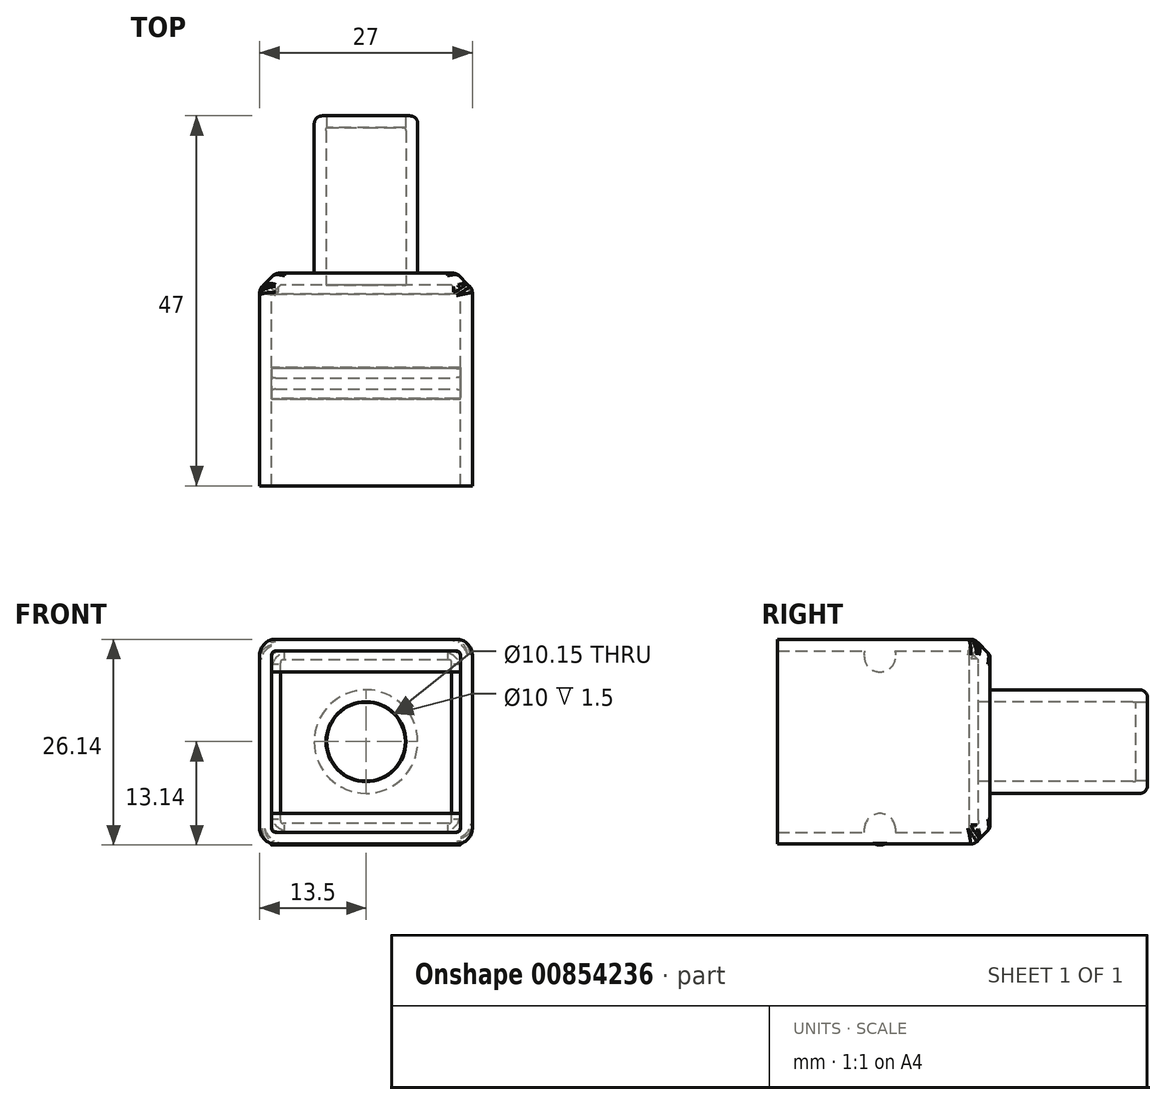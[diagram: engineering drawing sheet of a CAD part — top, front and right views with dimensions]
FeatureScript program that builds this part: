
annotation { "Feature Type Name" : "Feature", "Feature Type Description" : "" }
export const myFeature = defineFeature(function(context is Context, id is Id, definition is map)
    precondition{}
    {
        {
            var Q0;
            Q0=qCreatedBy(makeId("Front.planeOp"),FACE);
            var sketch = newSketch(context, id + "F0", { "sketchPlane" : qUnion([Q0])});
            skLineSegment(sketch, "E0.bottom", {"start": v(13.5, -13) * mm, "end": v(-13.5, -13) * mm});
            skLineSegment(sketch, "E0.top", {"start": v(13.5, 13) * mm, "end": v(-13.5, 13) * mm});
            skLineSegment(sketch, "E0.left", {"start": v(13.5, -13) * mm, "end": v(13.5, 13) * mm});
            skLineSegment(sketch, "E0.right", {"start": v(-13.5, -13) * mm, "end": v(-13.5, 13) * mm});
            skPoint(sketch, "E0.middle", {"position": v(0, 0) * mm});
            skSolve(sketch);
        }
        {
            var Q0;
            Q0=makeQuery(id+"F0.imprint","IMPRINT",FACE,{"disambiguationData":[TD([[makeQuery(id+"F0.imprint","IMPRINT",EDGE,{"derivedFrom":sQuery(id+"F0.wireOp",EDGE,"E0.bottom")}),-1.0]])]});
            extrude(context, id + "F1", {"entities" : qUnion([Q0]), "depth" : 27 * mm, "offsetDistance" : 25 * mm});
        }
        {
            var Q0;
            Q0=qCreatedBy(makeId("Front.planeOp"),FACE);
            var sketch = newSketch(context, id + "F2", { "sketchPlane" : qUnion([Q0])});
            skCircle(sketch, "E1", {"center": v(0, 0) * mm, "radius": 6.58 * mm});
            skSolve(sketch);
        }
        {
            var Q0;
            Q0=makeQuery(id+"F2.imprint","IMPRINT",FACE,{"disambiguationData":[TD([[makeQuery(id+"F2.imprint","IMPRINT",EDGE,{"derivedFrom":sQuery(id+"F2.wireOp",EDGE,"E1")}),1.0]])]});
            extrude(context, id + "F3", {"entities" : qUnion([Q0]), "operationType" : NewBodyOperationType.ADD, "oppositeDirection" : true, "depth" : 20 * mm, "offsetDistance" : 25 * mm});
        }
        {
            var Q0;
            Q0=makeQuery(id+"F3.opExtrude","CAP_EDGE",EDGE,{"disambiguationData":[OSD([sQuery(id+"F2.wireOp",EDGE,"E1")])],"isStart":false});
            fillet(context, id + "F4", {"entities" : qUnion([Q0]), "radius" : 1 * mm, "tangentPropagation" : true, "allowEdgeOverflow" : false});
        }
        {
            var Q0;
            Q0=makeQuery(id+"F1.opExtrude","CAP_EDGE",EDGE,{"disambiguationData":[OSD([sQuery(id+"F0.wireOp",EDGE,"E0.left")])],"isStart":true});
            var Q1;
            Q1=makeQuery(id+"F1.opExtrude","CAP_EDGE",EDGE,{"disambiguationData":[OSD([sQuery(id+"F0.wireOp",EDGE,"E0.bottom")])],"isStart":true});
            var Q2;
            Q2=makeQuery(id+"F1.opExtrude","CAP_EDGE",EDGE,{"disambiguationData":[OSD([sQuery(id+"F0.wireOp",EDGE,"E0.right")])],"isStart":true});
            var Q3;
            Q3=makeQuery(id+"F1.opExtrude","CAP_EDGE",EDGE,{"disambiguationData":[OSD([sQuery(id+"F0.wireOp",EDGE,"E0.top")])],"isStart":true});
            chamfer(context, id + "F5", {"entities" : qUnion([Q0, Q1, Q2, Q3]), "width" : 2 * mm, "tangentPropagation" : true});
        }
        {
            var Q0;
            {var subQ0=sQuery(id+"F0.wireOp",EDGE,"E0.right");Q0=makeQuery(id+"F5.opChamfer","BLEND_EDGE",EDGE,{"blendedFrom":[makeQuery(id+"F1.opExtrude","CAP_EDGE",EDGE,{"disambiguationData":[OSD([subQ0])],"isStart":true}),makeQuery(id+"F1.opExtrude","CAP_FACE",FACE,{"disambiguationData":[OSD([sQuery(id+"F0.wireOp",EDGE,"E0.bottom"),sQuery(id+"F0.wireOp",EDGE,"E0.top"),sQuery(id+"F0.wireOp",EDGE,"E0.left"),subQ0])],"isStart":true})],"blendedInto":[makeQuery(id+"F1.opExtrude","CAP_FACE",FACE,{"disambiguationData":[OSD([sQuery(id+"F0.wireOp",EDGE,"E0.bottom"),sQuery(id+"F0.wireOp",EDGE,"E0.top"),sQuery(id+"F0.wireOp",EDGE,"E0.left"),subQ0])],"isStart":true})]});}
            var Q1;
            {var subQ0=sQuery(id+"F0.wireOp",EDGE,"E0.bottom");Q1=makeQuery(id+"F5.opChamfer","BLEND_EDGE",EDGE,{"blendedFrom":[makeQuery(id+"F1.opExtrude","CAP_EDGE",EDGE,{"disambiguationData":[OSD([subQ0])],"isStart":true}),makeQuery(id+"F1.opExtrude","CAP_FACE",FACE,{"disambiguationData":[OSD([subQ0,sQuery(id+"F0.wireOp",EDGE,"E0.top"),sQuery(id+"F0.wireOp",EDGE,"E0.left"),sQuery(id+"F0.wireOp",EDGE,"E0.right")])],"isStart":true})],"blendedInto":[makeQuery(id+"F1.opExtrude","CAP_FACE",FACE,{"disambiguationData":[OSD([subQ0,sQuery(id+"F0.wireOp",EDGE,"E0.top"),sQuery(id+"F0.wireOp",EDGE,"E0.left"),sQuery(id+"F0.wireOp",EDGE,"E0.right")])],"isStart":true})]});}
            var Q2;
            {var subQ0=sQuery(id+"F0.wireOp",EDGE,"E0.left");Q2=makeQuery(id+"F5.opChamfer","BLEND_EDGE",EDGE,{"blendedFrom":[makeQuery(id+"F1.opExtrude","CAP_EDGE",EDGE,{"disambiguationData":[OSD([subQ0])],"isStart":true}),makeQuery(id+"F1.opExtrude","CAP_FACE",FACE,{"disambiguationData":[OSD([sQuery(id+"F0.wireOp",EDGE,"E0.bottom"),sQuery(id+"F0.wireOp",EDGE,"E0.top"),subQ0,sQuery(id+"F0.wireOp",EDGE,"E0.right")])],"isStart":true})],"blendedInto":[makeQuery(id+"F1.opExtrude","CAP_FACE",FACE,{"disambiguationData":[OSD([sQuery(id+"F0.wireOp",EDGE,"E0.bottom"),sQuery(id+"F0.wireOp",EDGE,"E0.top"),subQ0,sQuery(id+"F0.wireOp",EDGE,"E0.right")])],"isStart":true})]});}
            var Q3;
            {var subQ0=sQuery(id+"F0.wireOp",EDGE,"E0.top");Q3=makeQuery(id+"F5.opChamfer","BLEND_EDGE",EDGE,{"blendedFrom":[makeQuery(id+"F1.opExtrude","CAP_EDGE",EDGE,{"disambiguationData":[OSD([subQ0])],"isStart":true}),makeQuery(id+"F1.opExtrude","CAP_FACE",FACE,{"disambiguationData":[OSD([sQuery(id+"F0.wireOp",EDGE,"E0.bottom"),subQ0,sQuery(id+"F0.wireOp",EDGE,"E0.left"),sQuery(id+"F0.wireOp",EDGE,"E0.right")])],"isStart":true})],"blendedInto":[makeQuery(id+"F1.opExtrude","CAP_FACE",FACE,{"disambiguationData":[OSD([sQuery(id+"F0.wireOp",EDGE,"E0.bottom"),subQ0,sQuery(id+"F0.wireOp",EDGE,"E0.left"),sQuery(id+"F0.wireOp",EDGE,"E0.right")])],"isStart":true})]});}
            fillet(context, id + "F6", {"entities" : qUnion([Q0, Q1, Q2, Q3]), "radius" : 1 * mm, "tangentPropagation" : true, "allowEdgeOverflow" : false});
        }
        {
            var Q0;
            {var subQ0=sQuery(id+"F0.wireOp",EDGE,"E0.top");Q0=makeQuery(id+"F5.opChamfer","BLEND_EDGE",EDGE,{"blendedFrom":[makeQuery(id+"F1.opExtrude","CAP_EDGE",EDGE,{"disambiguationData":[OSD([subQ0])],"isStart":true}),makeQuery(id+"F1.opExtrude","SWEPT_FACE",FACE,{"disambiguationData":[OSD([subQ0])]})],"blendedInto":[makeQuery(id+"F1.opExtrude","SWEPT_FACE",FACE,{"disambiguationData":[OSD([subQ0])]})]});}
            var Q1;
            {var subQ0=sQuery(id+"F0.wireOp",EDGE,"E0.left");Q1=makeQuery(id+"F5.opChamfer","BLEND_EDGE",EDGE,{"blendedFrom":[makeQuery(id+"F1.opExtrude","CAP_EDGE",EDGE,{"disambiguationData":[OSD([subQ0])],"isStart":true}),makeQuery(id+"F1.opExtrude","SWEPT_FACE",FACE,{"disambiguationData":[OSD([subQ0])]})],"blendedInto":[makeQuery(id+"F1.opExtrude","SWEPT_FACE",FACE,{"disambiguationData":[OSD([subQ0])]})]});}
            var Q2;
            {var subQ0=sQuery(id+"F0.wireOp",EDGE,"E0.bottom");Q2=makeQuery(id+"F5.opChamfer","BLEND_EDGE",EDGE,{"blendedFrom":[makeQuery(id+"F1.opExtrude","CAP_EDGE",EDGE,{"disambiguationData":[OSD([subQ0])],"isStart":true}),makeQuery(id+"F1.opExtrude","SWEPT_FACE",FACE,{"disambiguationData":[OSD([subQ0])]})],"blendedInto":[makeQuery(id+"F1.opExtrude","SWEPT_FACE",FACE,{"disambiguationData":[OSD([subQ0])]})]});}
            var Q3;
            {var subQ0=sQuery(id+"F0.wireOp",EDGE,"E0.right");Q3=makeQuery(id+"F5.opChamfer","BLEND_EDGE",EDGE,{"blendedFrom":[makeQuery(id+"F1.opExtrude","CAP_EDGE",EDGE,{"disambiguationData":[OSD([subQ0])],"isStart":true}),makeQuery(id+"F1.opExtrude","SWEPT_FACE",FACE,{"disambiguationData":[OSD([subQ0])]})],"blendedInto":[makeQuery(id+"F1.opExtrude","SWEPT_FACE",FACE,{"disambiguationData":[OSD([subQ0])]})]});}
            fillet(context, id + "F7", {"entities" : qUnion([Q0, Q1, Q2, Q3]), "radius" : 1 * mm, "tangentPropagation" : true, "allowEdgeOverflow" : false});
        }
        {
            var Q0;
            Q0=makeQuery(id+"F1.opExtrude","SWEPT_EDGE",EDGE,{"disambiguationData":[OSD([sQuery(id+"F0.wireOp",EDGE,"E0.top"),sQuery(id+"F0.wireOp",EDGE,"E0.left")])]});
            var Q1;
            Q1=makeQuery(id+"F1.opExtrude","SWEPT_EDGE",EDGE,{"disambiguationData":[OSD([sQuery(id+"F0.wireOp",EDGE,"E0.bottom"),sQuery(id+"F0.wireOp",EDGE,"E0.left")])]});
            var Q2;
            Q2=makeQuery(id+"F1.opExtrude","SWEPT_EDGE",EDGE,{"disambiguationData":[OSD([sQuery(id+"F0.wireOp",EDGE,"E0.bottom"),sQuery(id+"F0.wireOp",EDGE,"E0.right")])]});
            var Q3;
            Q3=makeQuery(id+"F1.opExtrude","SWEPT_EDGE",EDGE,{"disambiguationData":[OSD([sQuery(id+"F0.wireOp",EDGE,"E0.top"),sQuery(id+"F0.wireOp",EDGE,"E0.right")])]});
            fillet(context, id + "F8", {"entities" : qUnion([Q0, Q1, Q2, Q3]), "radius" : 2 * mm, "tangentPropagation" : true, "allowEdgeOverflow" : false});
        }
        {
            var Q0;
            Q0=makeQuery(id+"F1.opExtrude","CAP_FACE",FACE,{"disambiguationData":[OSD([sQuery(id+"F0.wireOp",EDGE,"E0.bottom"),sQuery(id+"F0.wireOp",EDGE,"E0.top"),sQuery(id+"F0.wireOp",EDGE,"E0.left"),sQuery(id+"F0.wireOp",EDGE,"E0.right")])],"isStart":false});
            shell(context, id + "F9", {"entities" : qUnion([Q0]), "thickness" : 1.5 * mm});
        }
        {
            var Q0;
            Q0=qCreatedBy(makeId("Front.planeOp"),FACE);
            var sketch = newSketch(context, id + "F10", { "sketchPlane" : qUnion([Q0])});
            skPoint(sketch, "E2", {"position": v(0, 0) * mm});
            skSolve(sketch);
        }
        {
            var Q0;
            Q0=sQuery(id+"F10.wireOp",VERTEX,"E2");
            var Q1;
            Q1=makeQuery(id+"F1.opExtrude","SWEPT_BODY",BODY,{"disambiguationData":[OSD([sQuery(id+"F0.wireOp",EDGE,"E0.bottom"),sQuery(id+"F0.wireOp",EDGE,"E0.top"),sQuery(id+"F0.wireOp",EDGE,"E0.left"),sQuery(id+"F0.wireOp",EDGE,"E0.right")])]});
            hole(context, id + "F11", {"style" : HoleStyle.SIMPLE, "endStyle" : HoleEndStyle.THROUGH, "holeDiameter" : 10 * mm, "majorDiameter" : 5 * mm, "isTappedThrough" : true, "tappedDepth" : 12 * mm, "tapClearance" : 3, "locations" : qUnion([Q0]), "scope" : qUnion([Q1])});
        }
        {
            var Q0;
            Q0=qCreatedBy(makeId("Right.planeOp"),FACE);
            var sketch = newSketch(context, id + "F12", { "sketchPlane" : qUnion([Q0])});
            skCircle(sketch, "E3", {"center": v(-14, -11.14) * mm, "radius": 2 * mm});
            skSolve(sketch);
        }
        {
            var Q0;
            Q0 = qSketchRegion(id + "F12", true);
            extrude(context, id + "F13", {"entities" : qUnion([Q0]), "operationType" : NewBodyOperationType.ADD, "oppositeDirection" : true, "depth" : 12 * mm, "offsetDistance" : 25 * mm});
        }
        {
            var Q0;
            Q0 = qSketchRegion(id + "F12", true);
            extrude(context, id + "F14", {"entities" : qUnion([Q0]), "operationType" : NewBodyOperationType.ADD, "depth" : 12 * mm, "offsetDistance" : 25 * mm});
        }
        {
            var Q0;
            Q0=qCreatedBy(makeId("Right.planeOp"),FACE);
            var sketch = newSketch(context, id + "F15", { "sketchPlane" : qUnion([Q0])});
            skCircle(sketch, "E4", {"center": v(-14, 10.85) * mm, "radius": 2 * mm});
            skSolve(sketch);
        }
        {
            var Q0;
            Q0 = qSketchRegion(id + "F15", true);
            extrude(context, id + "F16", {"entities" : qUnion([Q0]), "operationType" : NewBodyOperationType.ADD, "depth" : 12 * mm, "offsetDistance" : 25 * mm});
        }
        {
            var Q0;
            Q0 = qSketchRegion(id + "F15", true);
            extrude(context, id + "F17", {"entities" : qUnion([Q0]), "operationType" : NewBodyOperationType.ADD, "oppositeDirection" : true, "depth" : 12 * mm, "offsetDistance" : 25 * mm});
        }
        {
            var Q0;
            {var subQ0=sQuery(id+"F2.wireOp",EDGE,"E1");Q0=makeQuery(id+"F9.opShell","OFFSET_EDGE",EDGE,{"disambiguationData":[OSD([subQ0]),TDD([makeQuery(id+"F3.opExtrude","CAP_EDGE",EDGE,{"disambiguationData":[OSD([subQ0])],"isStart":true})])]});}
            fillet(context, id + "F18", {"entities" : qUnion([Q0]), "radius" : 1 * mm, "tangentPropagation" : true, "allowEdgeOverflow" : false});
        }
    });
